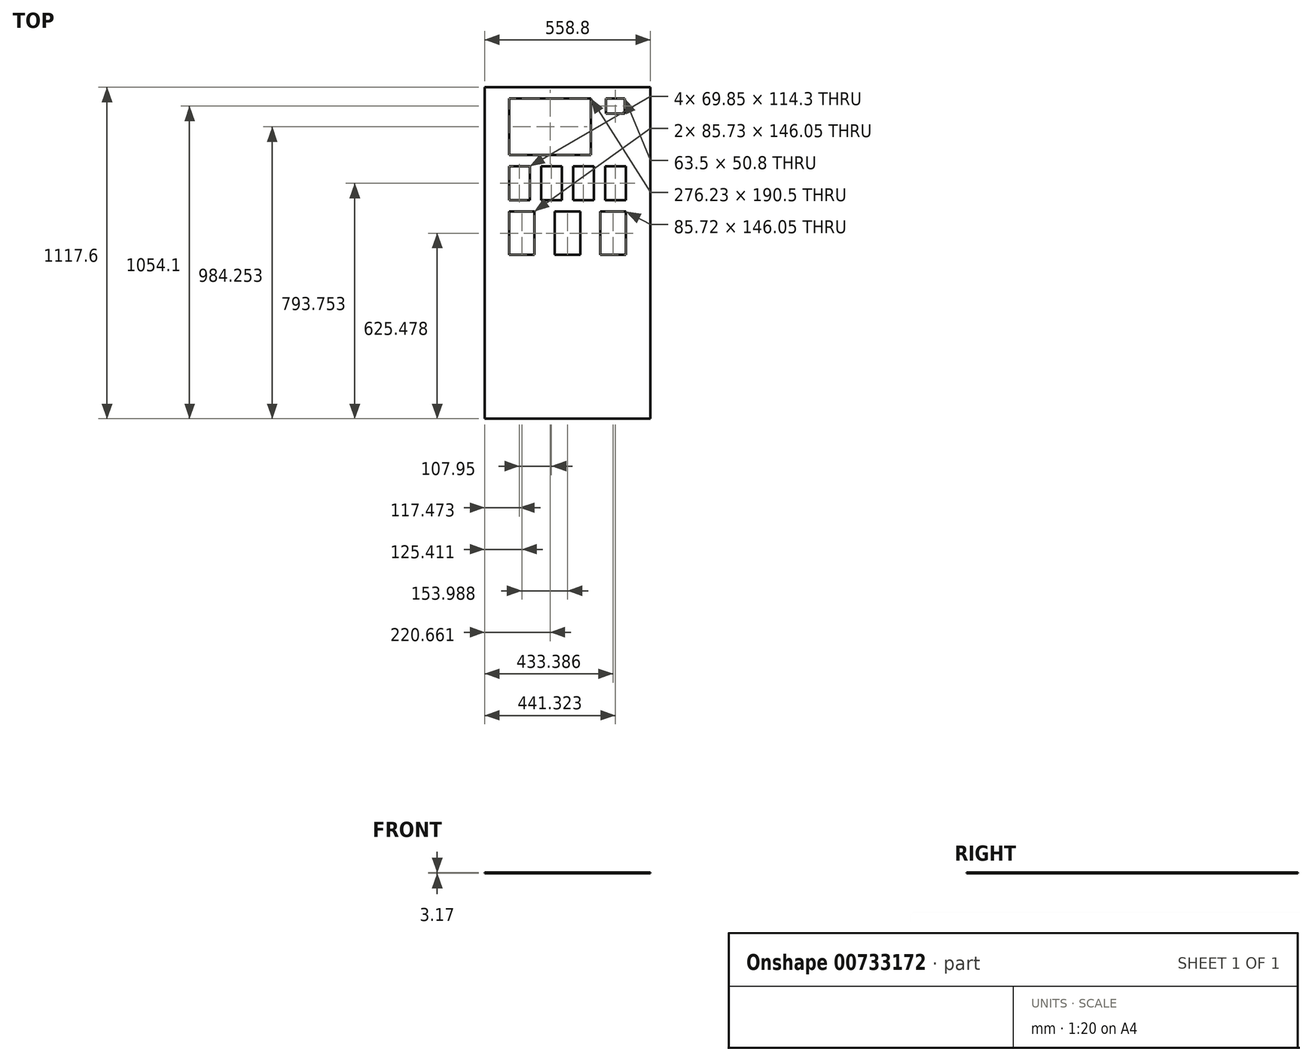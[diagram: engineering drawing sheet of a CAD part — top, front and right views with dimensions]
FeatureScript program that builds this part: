
annotation { "Feature Type Name" : "Feature", "Feature Type Description" : "" }
export const myFeature = defineFeature(function(context is Context, id is Id, definition is map)
    precondition{}
    {
        {
            var Q0;
            Q0=qCreatedBy(makeId("Top.planeOp"),FACE);
            var sketch = newSketch(context, id + "F0", { "sketchPlane" : qUnion([Q0])});
            skLineSegment(sketch, "E0.bottom", {"start": v(-188.71, 466.16) * mm, "end": v(-118.86, 466.16) * mm});
            skLineSegment(sketch, "E0.top", {"start": v(-188.71, 351.86) * mm, "end": v(-118.86, 351.86) * mm});
            skLineSegment(sketch, "E0.left", {"start": v(-188.71, 466.16) * mm, "end": v(-188.71, 351.86) * mm});
            skLineSegment(sketch, "E0.right", {"start": v(-118.86, 466.16) * mm, "end": v(-118.86, 351.86) * mm});
            skLineSegment(sketch, "E1.bottom", {"start": v(-250.62, 313.76) * mm, "end": v(-164.9, 313.76) * mm});
            skLineSegment(sketch, "E1.top", {"start": v(-250.62, 167.71) * mm, "end": v(-164.9, 167.71) * mm});
            skLineSegment(sketch, "E1.left", {"start": v(-250.62, 313.76) * mm, "end": v(-250.62, 167.71) * mm});
            skLineSegment(sketch, "E1.right", {"start": v(-164.9, 313.76) * mm, "end": v(-164.9, 167.71) * mm});
            skLineSegment(sketch, "E2.bottom", {"start": v(-487.16, 732.86) * mm, "end": v(71.64, 732.86) * mm});
            skLineSegment(sketch, "E2.top", {"start": v(-487.16, -384.74) * mm, "end": v(71.64, -384.74) * mm});
            skLineSegment(sketch, "E2.left", {"start": v(-487.16, 732.86) * mm, "end": v(-487.16, -384.74) * mm});
            skLineSegment(sketch, "E2.right", {"start": v(71.64, 732.86) * mm, "end": v(71.64, -384.74) * mm});
            skLineSegment(sketch, "E3.bottom", {"start": v(-96.64, 313.76) * mm, "end": v(-10.91, 313.76) * mm});
            skLineSegment(sketch, "E3.top", {"start": v(-96.64, 167.71) * mm, "end": v(-10.91, 167.71) * mm});
            skLineSegment(sketch, "E3.left", {"start": v(-96.64, 313.76) * mm, "end": v(-96.64, 167.71) * mm});
            skLineSegment(sketch, "E3.right", {"start": v(-10.91, 313.76) * mm, "end": v(-10.91, 167.71) * mm});
            skLineSegment(sketch, "E4.bottom", {"start": v(-80.76, 466.16) * mm, "end": v(-10.91, 466.16) * mm});
            skLineSegment(sketch, "E4.top", {"start": v(-80.76, 351.86) * mm, "end": v(-10.91, 351.86) * mm});
            skLineSegment(sketch, "E4.left", {"start": v(-80.76, 466.16) * mm, "end": v(-80.76, 351.86) * mm});
            skLineSegment(sketch, "E4.right", {"start": v(-10.91, 466.16) * mm, "end": v(-10.91, 351.86) * mm});
            skLineSegment(sketch, "E5.bottom", {"start": v(-404.61, 694.76) * mm, "end": v(-128.39, 694.76) * mm});
            skLineSegment(sketch, "E5.top", {"start": v(-404.61, 504.26) * mm, "end": v(-128.39, 504.26) * mm});
            skLineSegment(sketch, "E5.left", {"start": v(-404.61, 694.76) * mm, "end": v(-404.61, 504.26) * mm});
            skLineSegment(sketch, "E5.right", {"start": v(-128.39, 694.76) * mm, "end": v(-128.39, 504.26) * mm});
            skLineSegment(sketch, "E6.bottom", {"start": v(-404.61, 313.76) * mm, "end": v(-318.89, 313.76) * mm});
            skLineSegment(sketch, "E6.top", {"start": v(-404.61, 167.71) * mm, "end": v(-318.89, 167.71) * mm});
            skLineSegment(sketch, "E6.left", {"start": v(-404.61, 313.76) * mm, "end": v(-404.61, 167.71) * mm});
            skLineSegment(sketch, "E6.right", {"start": v(-318.89, 313.76) * mm, "end": v(-318.89, 167.71) * mm});
            skLineSegment(sketch, "E7.bottom", {"start": v(-296.66, 466.16) * mm, "end": v(-226.81, 466.16) * mm});
            skLineSegment(sketch, "E7.top", {"start": v(-296.66, 351.86) * mm, "end": v(-226.81, 351.86) * mm});
            skLineSegment(sketch, "E7.left", {"start": v(-296.66, 466.16) * mm, "end": v(-296.66, 351.86) * mm});
            skLineSegment(sketch, "E7.right", {"start": v(-226.81, 466.16) * mm, "end": v(-226.81, 351.86) * mm});
            skLineSegment(sketch, "E8.bottom", {"start": v(-404.61, 466.16) * mm, "end": v(-334.76, 466.16) * mm});
            skLineSegment(sketch, "E8.top", {"start": v(-404.61, 351.86) * mm, "end": v(-334.76, 351.86) * mm});
            skLineSegment(sketch, "E8.left", {"start": v(-404.61, 466.16) * mm, "end": v(-404.61, 351.86) * mm});
            skLineSegment(sketch, "E8.right", {"start": v(-334.76, 466.16) * mm, "end": v(-334.76, 351.86) * mm});
            skLineSegment(sketch, "E9.bottom", {"start": v(-77.59, 694.76) * mm, "end": v(-14.09, 694.76) * mm});
            skLineSegment(sketch, "E9.top", {"start": v(-77.59, 643.96) * mm, "end": v(-14.09, 643.96) * mm});
            skLineSegment(sketch, "E9.left", {"start": v(-77.59, 694.76) * mm, "end": v(-77.59, 643.96) * mm});
            skLineSegment(sketch, "E9.right", {"start": v(-14.09, 694.76) * mm, "end": v(-14.09, 643.96) * mm});
            skSolve(sketch);
        }
        {
            var Q0;
            Q0=makeQuery(id+"F0.imprint","IMPRINT",FACE,{"disambiguationData":[TD([[makeQuery(id+"F0.imprint","IMPRINT",EDGE,{"derivedFrom":sQuery(id+"F0.wireOp",EDGE,"E0.bottom")}),1.0]])]});
            extrude(context, id + "F1", {"entities" : qUnion([Q0]), "depth" : 3.17 * mm, "offsetDistance" : 25.4 * mm});
        }
    });
